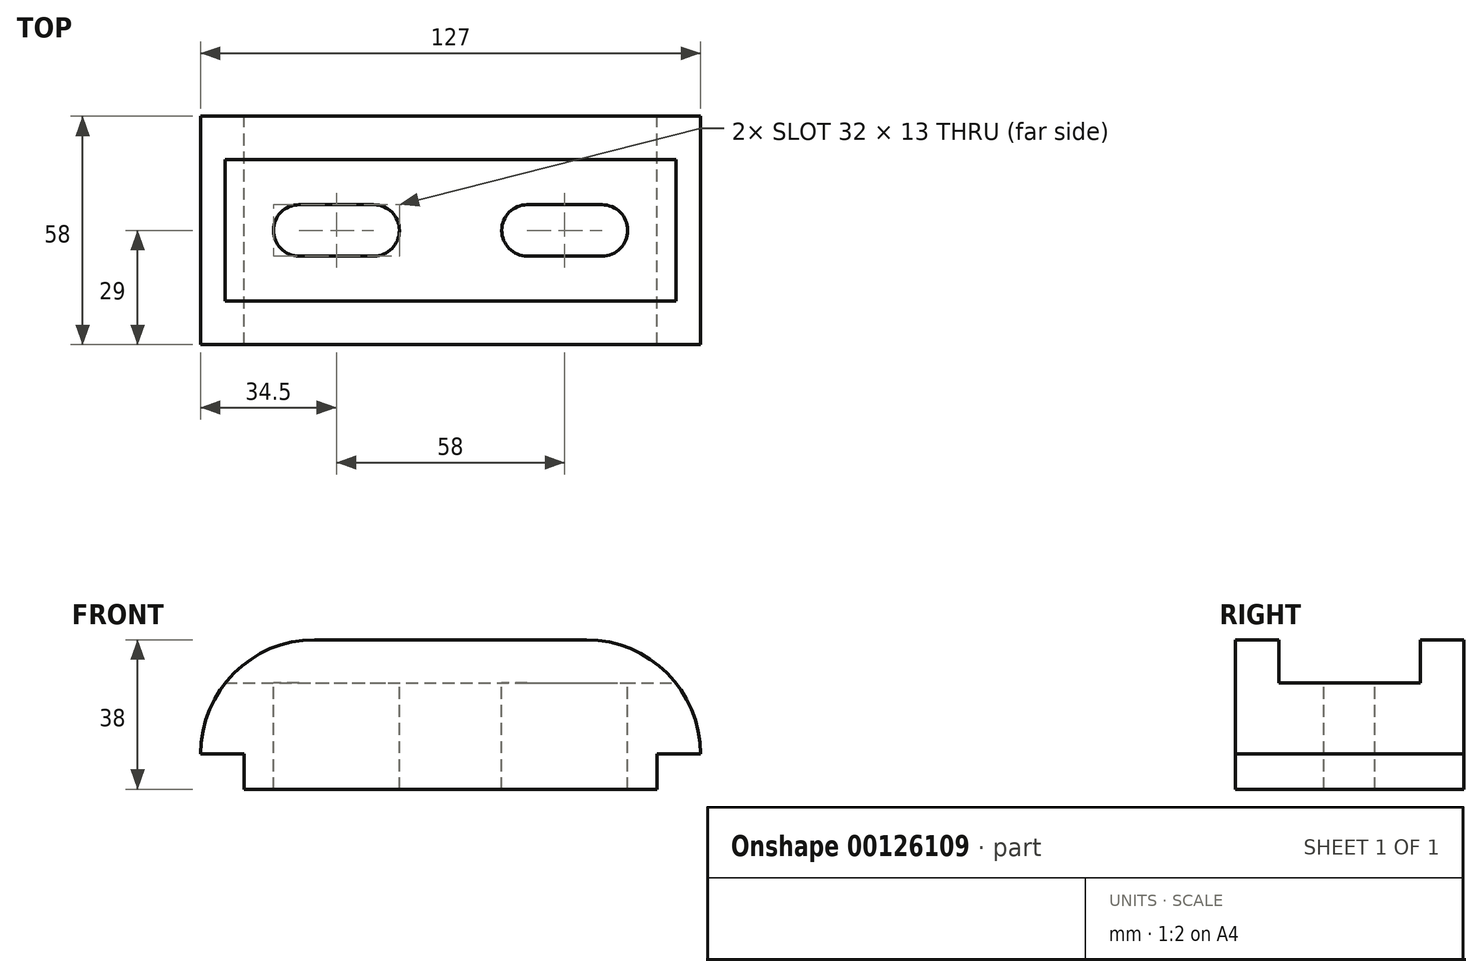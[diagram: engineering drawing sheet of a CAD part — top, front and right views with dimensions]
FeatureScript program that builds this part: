
annotation { "Feature Type Name" : "Feature", "Feature Type Description" : "" }
export const myFeature = defineFeature(function(context is Context, id is Id, definition is map)
    precondition{}
    {
        {
            var Q0;
            Q0=qCreatedBy(makeId("Front.planeOp"),FACE);
            var sketch = newSketch(context, id + "F0", { "sketchPlane" : qUnion([Q0])});
            skLineSegment(sketch, "E0", {"start": v(-63.5, 9) * mm, "end": v(-52.5, 9) * mm});
            skLineSegment(sketch, "E1", {"start": v(-52.5, 9) * mm, "end": v(-52.5, 0) * mm});
            skLineSegment(sketch, "E2", {"start": v(-52.5, 0) * mm, "end": v(52.5, 0) * mm});
            skLineSegment(sketch, "E3", {"start": v(52.5, 0) * mm, "end": v(52.5, 9) * mm});
            skLineSegment(sketch, "E4", {"start": v(52.5, 9) * mm, "end": v(63.5, 9) * mm});
            skLineSegment(sketch, "E5", {"start": v(-34.5, 38) * mm, "end": v(34.5, 38) * mm});
            skArc(sketch, "E6", {"start": v(-63.5, 9) * mm, "mid": v(-55, 29.5) * mm, "end": v(-34.5, 38) * mm});
            skArc(sketch, "E7", {"start": v(34.5, 38) * mm, "mid": v(55, 29.5) * mm, "end": v(63.5, 9) * mm});
            skSolve(sketch);
        }
        {
            var Q0;
            Q0 = qSketchRegion(id + "F0", true);
            extrude(context, id + "F1", {"entities" : qUnion([Q0]), "depth" : 58 * mm});
        }
        {
            var Q0;
            Q0=makeQuery(id+"F1.opExtrude","SWEPT_FACE",FACE,{"disambiguationData":[OSD([sQuery(id+"F0.wireOp",EDGE,"E5")])]});
            var sketch = newSketch(context, id + "F2", { "sketchPlane" : qUnion([Q0])});
            skLineSegment(sketch, "E8", {"start": v(-63.5, -11) * mm, "end": v(63.5, -11) * mm});
            skLineSegment(sketch, "E9", {"start": v(63.5, -11) * mm, "end": v(63.5, -47) * mm});
            skLineSegment(sketch, "E10", {"start": v(-63.5, -11) * mm, "end": v(-63.5, -47) * mm});
            skLineSegment(sketch, "E11", {"start": v(-63.5, -47) * mm, "end": v(63.5, -47) * mm});
            skSolve(sketch);
        }
        {
            var Q0;
            Q0 = qSketchRegion(id + "F2", true);
            extrude(context, id + "F3", {"entities" : qUnion([Q0]), "operationType" : NewBodyOperationType.REMOVE, "oppositeDirection" : true, "depth" : 11 * mm});
        }
        {
            var Q0;
            Q0=makeQuery(id+"F3.boolean.opBoolean","COPY",FACE,{"derivedFrom":makeQuery(id+"F3.opExtrude","CAP_FACE",FACE,{"disambiguationData":[OSD([sQuery(id+"F2.wireOp",EDGE,"E8"),sQuery(id+"F2.wireOp",EDGE,"E9"),sQuery(id+"F2.wireOp",EDGE,"E10"),sQuery(id+"F2.wireOp",EDGE,"E11")])],"isStart":false})});
            var sketch = newSketch(context, id + "F4", { "sketchPlane" : qUnion([Q0])});
            skLineSegment(sketch, "E12", {"start": v(-38.5, -22.5) * mm, "end": v(-19.5, -22.5) * mm});
            skLineSegment(sketch, "E13", {"start": v(-38.5, -35.5) * mm, "end": v(-19.5, -35.5) * mm});
            skArc(sketch, "E14", {"start": v(-38.5, -22.5) * mm, "mid": v(-45, -29) * mm, "end": v(-38.5, -35.5) * mm});
            skArc(sketch, "E15", {"start": v(-19.5, -35.5) * mm, "mid": v(-13, -29) * mm, "end": v(-19.5, -22.5) * mm});
            skLineSegment(sketch, "E16", {"start": v(19.5, -22.5) * mm, "end": v(38.5, -22.5) * mm});
            skLineSegment(sketch, "E17", {"start": v(19.5, -35.5) * mm, "end": v(38.5, -35.5) * mm});
            skArc(sketch, "E18", {"start": v(19.5, -22.5) * mm, "mid": v(13, -29) * mm, "end": v(19.5, -35.5) * mm});
            skArc(sketch, "E19", {"start": v(38.5, -35.5) * mm, "mid": v(45, -29) * mm, "end": v(38.5, -22.5) * mm});
            skSolve(sketch);
        }
        {
            var Q0;
            Q0=makeQuery(id+"F4.imprint","IMPRINT",FACE,{"disambiguationData":[TD([[makeQuery(id+"F4.imprint","IMPRINT",EDGE,{"derivedFrom":sQuery(id+"F4.wireOp",EDGE,"E12")}),-1.0]])]});
            var Q1;
            Q1=makeQuery(id+"F4.imprint","IMPRINT",FACE,{"disambiguationData":[TD([[makeQuery(id+"F4.imprint","IMPRINT",EDGE,{"derivedFrom":sQuery(id+"F4.wireOp",EDGE,"E16")}),-1.0]])]});
            extrude(context, id + "F5", {"entities" : qUnion([Q0, Q1]), "operationType" : NewBodyOperationType.REMOVE, "endBound" : BoundingType.THROUGH_ALL, "oppositeDirection" : true, "depth" : 1.74 * mm});
        }
    });
